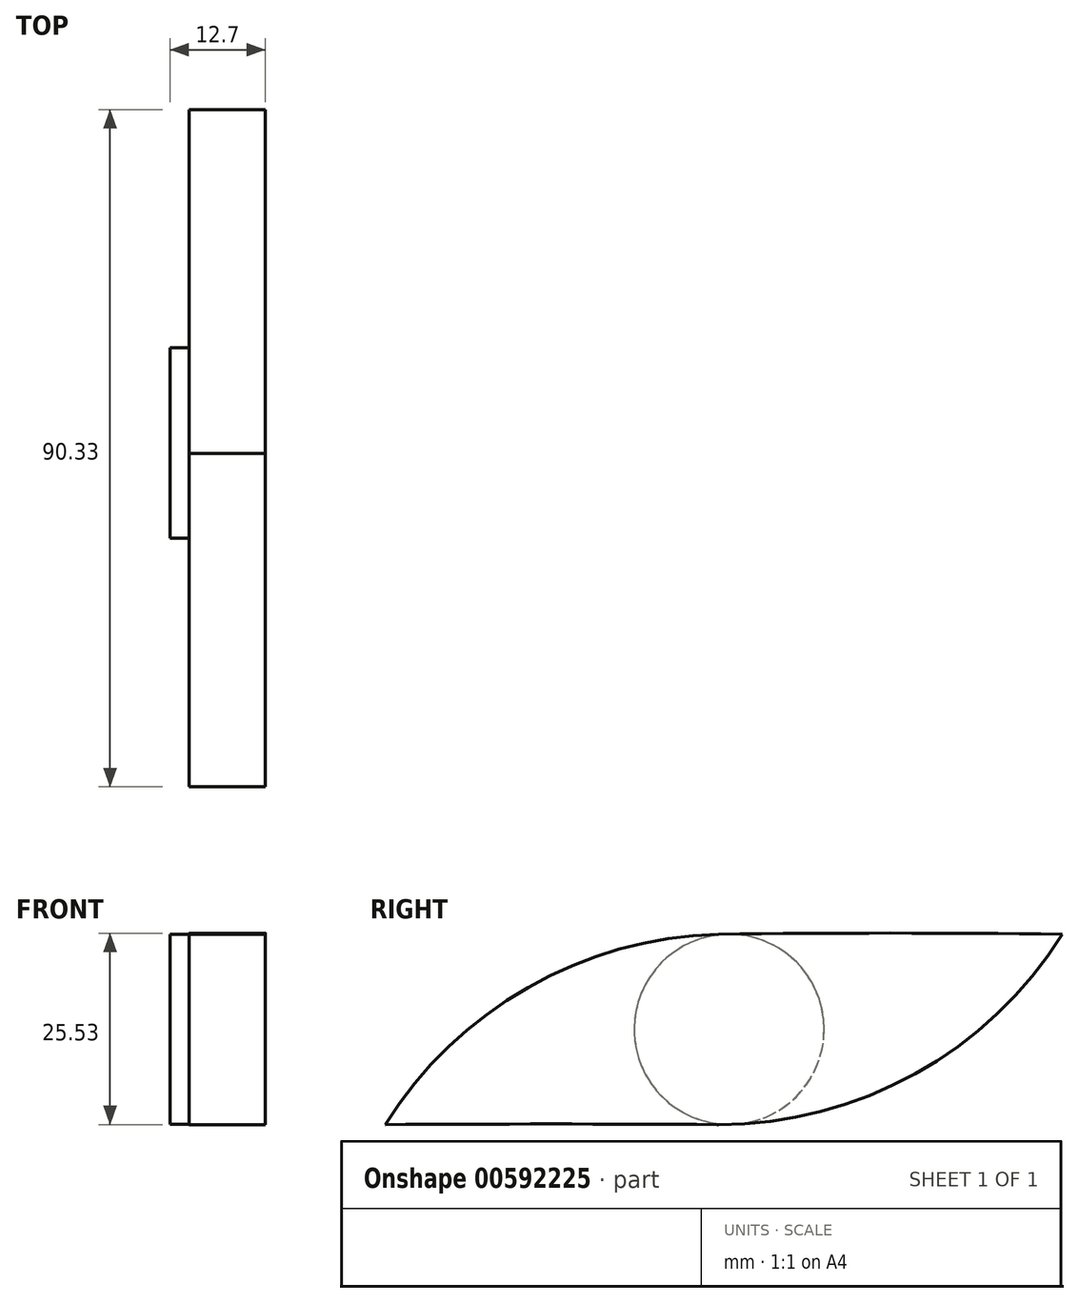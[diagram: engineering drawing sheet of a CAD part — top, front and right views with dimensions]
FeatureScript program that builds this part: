
annotation { "Feature Type Name" : "Feature", "Feature Type Description" : "" }
export const myFeature = defineFeature(function(context is Context, id is Id, definition is map)
    precondition{}
    {
        {
            var Q0;
            Q0=qCreatedBy(makeId("Right.planeOp"),FACE);
            var sketch = newSketch(context, id + "F0", { "sketchPlane" : qUnion([Q0])});
            skCircle(sketch, "E0", {"center": v(0, 0) * mm, "radius": 12.7 * mm});
            skLineSegment(sketch, "E1", {"start": v(0, 0) * mm, "end": v(-44.45, 0) * mm, "construction": true});
            skLineSegment(sketch, "E2", {"start": v(-44.45, 0) * mm, "end": v(-44.45, -12.7) * mm, "construction": true});
            skLineSegment(sketch, "E3", {"start": v(1.43, 0) * mm, "end": v(45.88, 0) * mm, "construction": true});
            skLineSegment(sketch, "E4", {"start": v(45.88, 0) * mm, "end": v(45.88, 12.7) * mm, "construction": true});
            skArc(sketch, "E5", {"start": v(0, -12.7) * mm, "mid": v(26.22, -5.93) * mm, "end": v(45.88, 12.7) * mm});
            skArc(sketch, "E6", {"start": v(45.88, 12.7) * mm, "mid": v(22.94, 12.83) * mm, "end": v(0, 12.7) * mm});
            skArc(sketch, "E7", {"start": v(0, 12.7) * mm, "mid": v(-25.42, 5.6) * mm, "end": v(-44.45, -12.7) * mm});
            skArc(sketch, "E8", {"start": v(0, -12.7) * mm, "mid": v(-22.23, -12.63) * mm, "end": v(-44.45, -12.7) * mm});
            skSolve(sketch);
        }
        {
            var Q0;
            {var subQ0=sQuery(id+"F0.wireOp",EDGE,"E0");var subQ1=makeQuery(id+"F0.imprint","INTERSECT",VERTEX,{"derivedFrom":[subQ0,sQuery(id+"F0.wireOp",EDGE,"E8")]});Q0=makeQuery(id+"F0.imprint","IMPRINT",FACE,{"disambiguationData":[TD([[makeQuery(id+"F0.imprint","IMPRINT",EDGE,{"disambiguationData":[TD([[subQ1,1.0]])],"derivedFrom":subQ0}),1.0]])]});}
            var Q1;
            {var subQ0=sQuery(id+"F0.wireOp",EDGE,"E5");Q1=makeQuery(id+"F0.imprint","IMPRINT",FACE,{"disambiguationData":[TD([[makeQuery(id+"F0.imprint","IMPRINT",EDGE,{"derivedFrom":subQ0}),1.0]])]});}
            var Q2;
            {var subQ0=sQuery(id+"F0.wireOp",EDGE,"E8");Q2=makeQuery(id+"F0.imprint","IMPRINT",FACE,{"disambiguationData":[TD([[makeQuery(id+"F0.imprint","IMPRINT",EDGE,{"derivedFrom":subQ0}),-1.0]])]});}
            extrude(context, id + "F1", {"entities" : qUnion([Q0, Q1, Q2]), "depth" : 10.16 * mm, "offsetDistance" : 25.4 * mm});
        }
        {
            var Q0;
            Q0=makeQuery(id+"F1.opExtrude","CAP_FACE",FACE,{"disambiguationData":[OSD([sQuery(id+"F0.wireOp",EDGE,"E0"),sQuery(id+"F0.wireOp",EDGE,"E5"),sQuery(id+"F0.wireOp",EDGE,"E6"),sQuery(id+"F0.wireOp",EDGE,"E7"),sQuery(id+"F0.wireOp",EDGE,"E8")])],"isStart":false});
            var sketch = newSketch(context, id + "F2", { "sketchPlane" : qUnion([Q0])});
            skCircle(sketch, "E9", {"center": v(1.43, 0) * mm, "radius": 12.68 * mm});
            skSolve(sketch);
        }
        {
            var Q0;
            Q0 = qSketchRegion(id + "F2", true);
            extrude(context, id + "F3", {"entities" : qUnion([Q0]), "operationType" : NewBodyOperationType.ADD, "oppositeDirection" : true, "depth" : 12.7 * mm, "offsetDistance" : 25.4 * mm});
        }
    });
